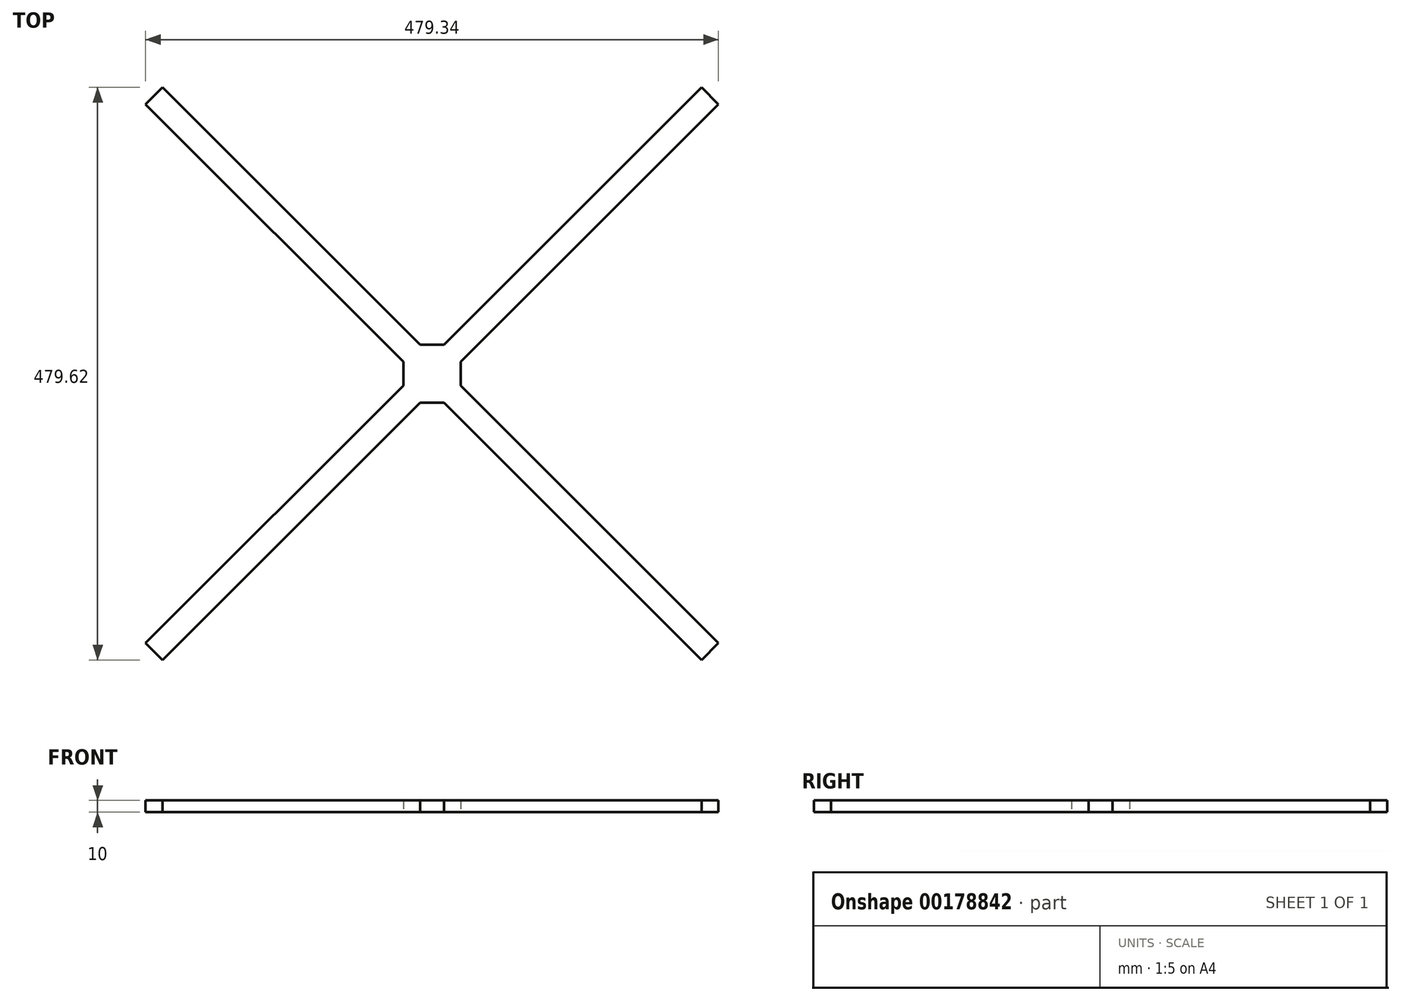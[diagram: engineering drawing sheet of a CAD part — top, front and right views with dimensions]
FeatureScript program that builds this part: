
annotation { "Feature Type Name" : "Feature", "Feature Type Description" : "" }
export const myFeature = defineFeature(function(context is Context, id is Id, definition is map)
    precondition{}
    {
        {
            var Q0;
            Q0=qCreatedBy(makeId("Top.planeOp"),FACE);
            var sketch = newSketch(context, id + "F0", { "sketchPlane" : qUnion([Q0])});
            skLineSegment(sketch, "E0.bottom", {"start": v(-10, 24.28) * mm, "end": v(10, 24.28) * mm});
            skLineSegment(sketch, "E0.top", {"start": v(-10, -24.28) * mm, "end": v(10, -24.28) * mm});
            skLineSegment(sketch, "E0.left", {"start": v(-24, 10) * mm, "end": v(-24, -10) * mm});
            skLineSegment(sketch, "E0.right", {"start": v(24, 10) * mm, "end": v(24, -10) * mm});
            skPoint(sketch, "E1", {"position": v(0, 0) * mm});
            skLineSegment(sketch, "E2", {"start": v(24, 10) * mm, "end": v(239.67, 225.67) * mm});
            skLineSegment(sketch, "E3", {"start": v(239.67, 225.67) * mm, "end": v(225.53, 239.8) * mm});
            skLineSegment(sketch, "E4", {"start": v(225.53, 239.8) * mm, "end": v(10, 24.28) * mm});
            skLineSegment(sketch, "E5", {"start": v(0, 239.8) * mm, "end": v(0, -104.47) * mm, "construction": true});
            skLineSegment(sketch, "E6.MirrorCS", {"start": v(-225.53, 239.8) * mm, "end": v(-10, 24.28) * mm});
            skLineSegment(sketch, "E7.MirrorCS", {"start": v(-239.67, 225.67) * mm, "end": v(-225.53, 239.8) * mm});
            skLineSegment(sketch, "E8.MirrorCS", {"start": v(-24, 10) * mm, "end": v(-239.67, 225.67) * mm});
            skLineSegment(sketch, "E9", {"start": v(-239.67, 0) * mm, "end": v(239.67, 0) * mm, "construction": true});
            skLineSegment(sketch, "E10.MirrorCS", {"start": v(-225.53, -239.8) * mm, "end": v(-10, -24.28) * mm});
            skLineSegment(sketch, "E11.MirrorCS", {"start": v(-239.67, -225.67) * mm, "end": v(-225.53, -239.8) * mm});
            skLineSegment(sketch, "E12.MirrorCS", {"start": v(-24, -10) * mm, "end": v(-239.67, -225.67) * mm});
            skLineSegment(sketch, "E13.MirrorCS", {"start": v(24, -10) * mm, "end": v(239.67, -225.67) * mm});
            skLineSegment(sketch, "E14.MirrorCS", {"start": v(225.53, -239.8) * mm, "end": v(10, -24.28) * mm});
            skLineSegment(sketch, "E15.MirrorCS", {"start": v(239.67, -225.67) * mm, "end": v(225.53, -239.8) * mm});
            skSolve(sketch);
        }
        {
            var Q0;
            Q0=makeQuery(id+"F0.imprint","IMPRINT",FACE,{"disambiguationData":[TD([[makeQuery(id+"F0.imprint","IMPRINT",EDGE,{"derivedFrom":sQuery(id+"F0.wireOp",EDGE,"E0.bottom")}),-1.0]])]});
            extrude(context, id + "F1", {"entities" : qUnion([Q0]), "depth" : 10 * mm});
        }
    });
